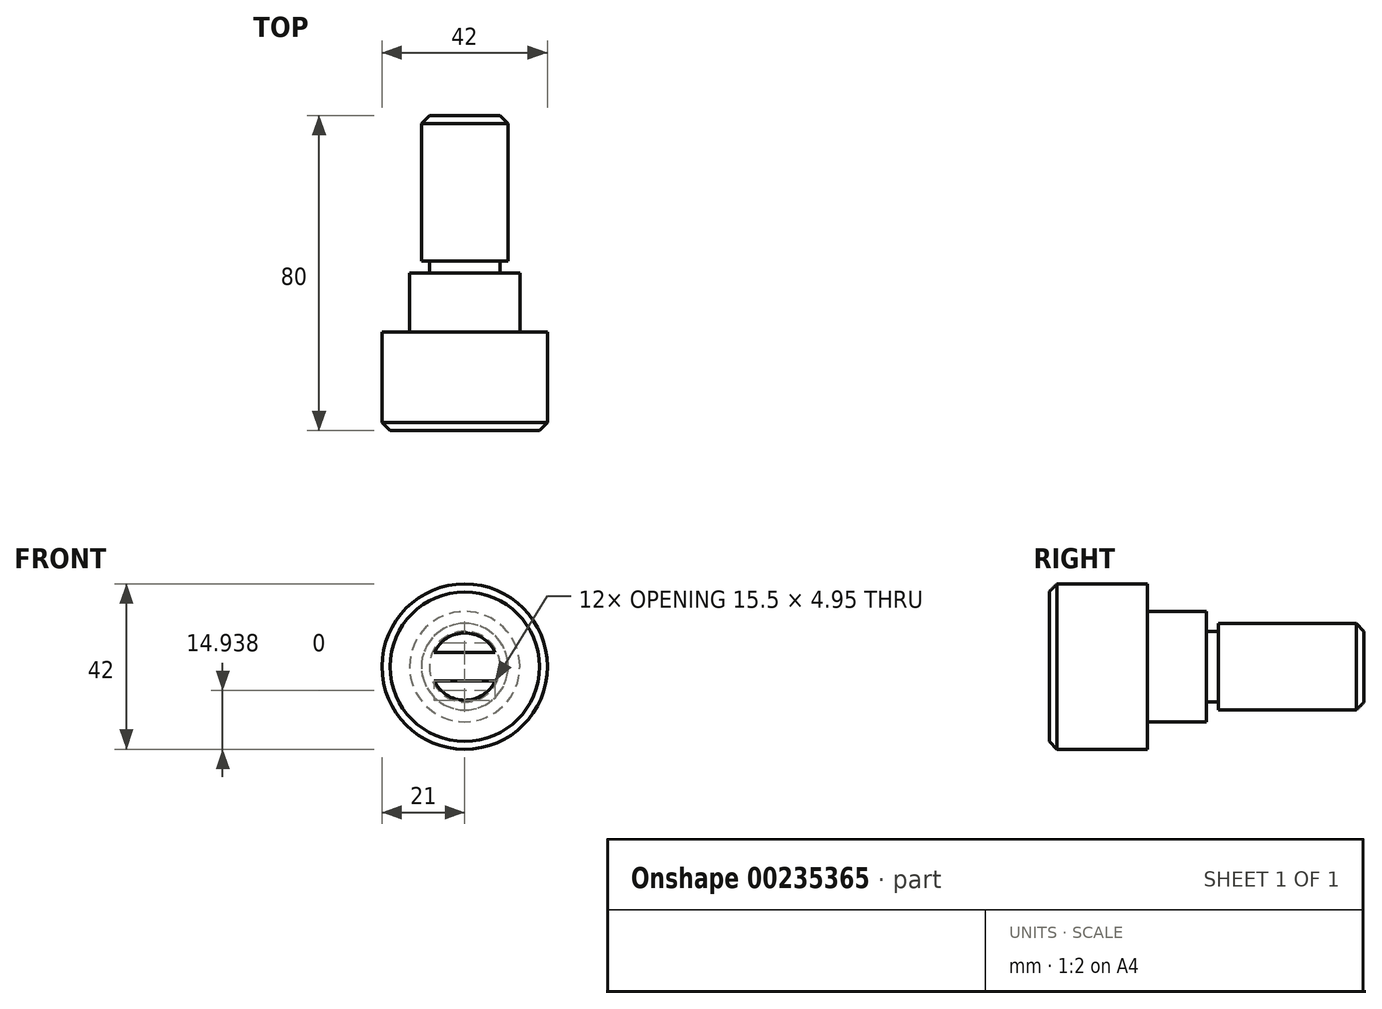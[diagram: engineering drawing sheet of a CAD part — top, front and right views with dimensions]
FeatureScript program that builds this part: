
annotation { "Feature Type Name" : "Feature", "Feature Type Description" : "" }
export const myFeature = defineFeature(function(context is Context, id is Id, definition is map)
    precondition{}
    {
        {
            var Q0;
            Q0=qCreatedBy(makeId("Top.planeOp"),FACE);
            var sketch = newSketch(context, id + "F0", { "sketchPlane" : qUnion([Q0])});
            skLineSegment(sketch, "E0", {"start": v(0, 0) * mm, "end": v(21, 0) * mm});
            skLineSegment(sketch, "E1", {"start": v(21, 0) * mm, "end": v(21, 25) * mm});
            skLineSegment(sketch, "E2", {"start": v(21, 25) * mm, "end": v(14, 25) * mm});
            skLineSegment(sketch, "E3", {"start": v(14, 25) * mm, "end": v(14, 40) * mm});
            skLineSegment(sketch, "E4", {"start": v(14, 40) * mm, "end": v(9, 40) * mm});
            skLineSegment(sketch, "E5", {"start": v(9, 40) * mm, "end": v(9, 43) * mm});
            skLineSegment(sketch, "E6", {"start": v(9, 43) * mm, "end": v(11, 43) * mm});
            skLineSegment(sketch, "E7", {"start": v(11, 43) * mm, "end": v(11, 80) * mm});
            skLineSegment(sketch, "E8", {"start": v(11, 80) * mm, "end": v(0, 80) * mm});
            skLineSegment(sketch, "E9", {"start": v(0, 80) * mm, "end": v(0, 0) * mm});
            skSolve(sketch);
        }
        {
            var Q0;
            Q0=makeQuery(id+"F0.imprint","IMPRINT",FACE,{"disambiguationData":[TD([[makeQuery(id+"F0.imprint","IMPRINT",EDGE,{"derivedFrom":sQuery(id+"F0.wireOp",EDGE,"E0")}),1.0]])]});
            var Q1;
            Q1=sQuery(id+"F0.wireOp",EDGE,"E9");
            revolve(context, id + "F1", {"entities" : qUnion([Q0]), "axis" : qUnion([Q1]), "revolveType" : RevolveType.FULL});
        }
        {
            var Q0;
            Q0=makeQuery(id+"F1.opRevolve","SWEPT_EDGE",EDGE,{"disambiguationData":[OSD([sQuery(id+"F0.wireOp",EDGE,"E8"),sQuery(id+"F0.wireOp",EDGE,"E7")])]});
            var Q1;
            Q1=makeQuery(id+"F1.opRevolve","SWEPT_EDGE",EDGE,{"disambiguationData":[OSD([sQuery(id+"F0.wireOp",EDGE,"E0"),sQuery(id+"F0.wireOp",EDGE,"E1")])]});
            chamfer(context, id + "F2", {"entities" : qUnion([Q0, Q1]), "chamferType" : ChamferType.OFFSET_ANGLE, "width" : 2 * mm, "oppositeDirection" : false, "angle" : 45 * degree, "tangentPropagation" : true});
        }
        {
            var Q0;
            Q0=qCreatedBy(makeId("Front.planeOp"),FACE);
            var sketch = newSketch(context, id + "F3", { "sketchPlane" : qUnion([Q0])});
            skPoint(sketch, "E10", {"position": v(0, 0) * mm});
            skLineSegment(sketch, "E11.bottom", {"start": v(7.75, 3.58) * mm, "end": v(-7.75, 3.58) * mm});
            skLineSegment(sketch, "E11.top", {"start": v(7.75, -3.58) * mm, "end": v(-7.75, -3.58) * mm});
            skLineSegment(sketch, "E11.left", {"start": v(7.75, 3.58) * mm, "end": v(7.75, -3.58) * mm});
            skLineSegment(sketch, "E11.right", {"start": v(-7.75, 3.58) * mm, "end": v(-7.75, -3.58) * mm});
            skCircle(sketch, "E12", {"center": v(0, 0) * mm, "radius": 8.54 * mm});
            skSolve(sketch);
        }
        {
            var Q0;
            {var subQ0=sQuery(id+"F3.wireOp",EDGE,"E11.bottom");Q0=makeQuery(id+"F3.imprint","IMPRINT",FACE,{"disambiguationData":[TD([[makeQuery(id+"F3.imprint","IMPRINT",EDGE,{"derivedFrom":subQ0}),-1.0]])]});}
            var Q1;
            {var subQ0=sQuery(id+"F3.wireOp",EDGE,"E11.top");Q1=makeQuery(id+"F3.imprint","IMPRINT",FACE,{"disambiguationData":[TD([[makeQuery(id+"F3.imprint","IMPRINT",EDGE,{"derivedFrom":subQ0}),1.0]])]});}
            extrude(context, id + "F4", {"entities" : qUnion([Q0, Q1]), "operationType" : NewBodyOperationType.REMOVE, "oppositeDirection" : true, "depth" : 100 * mm});
        }
    });
